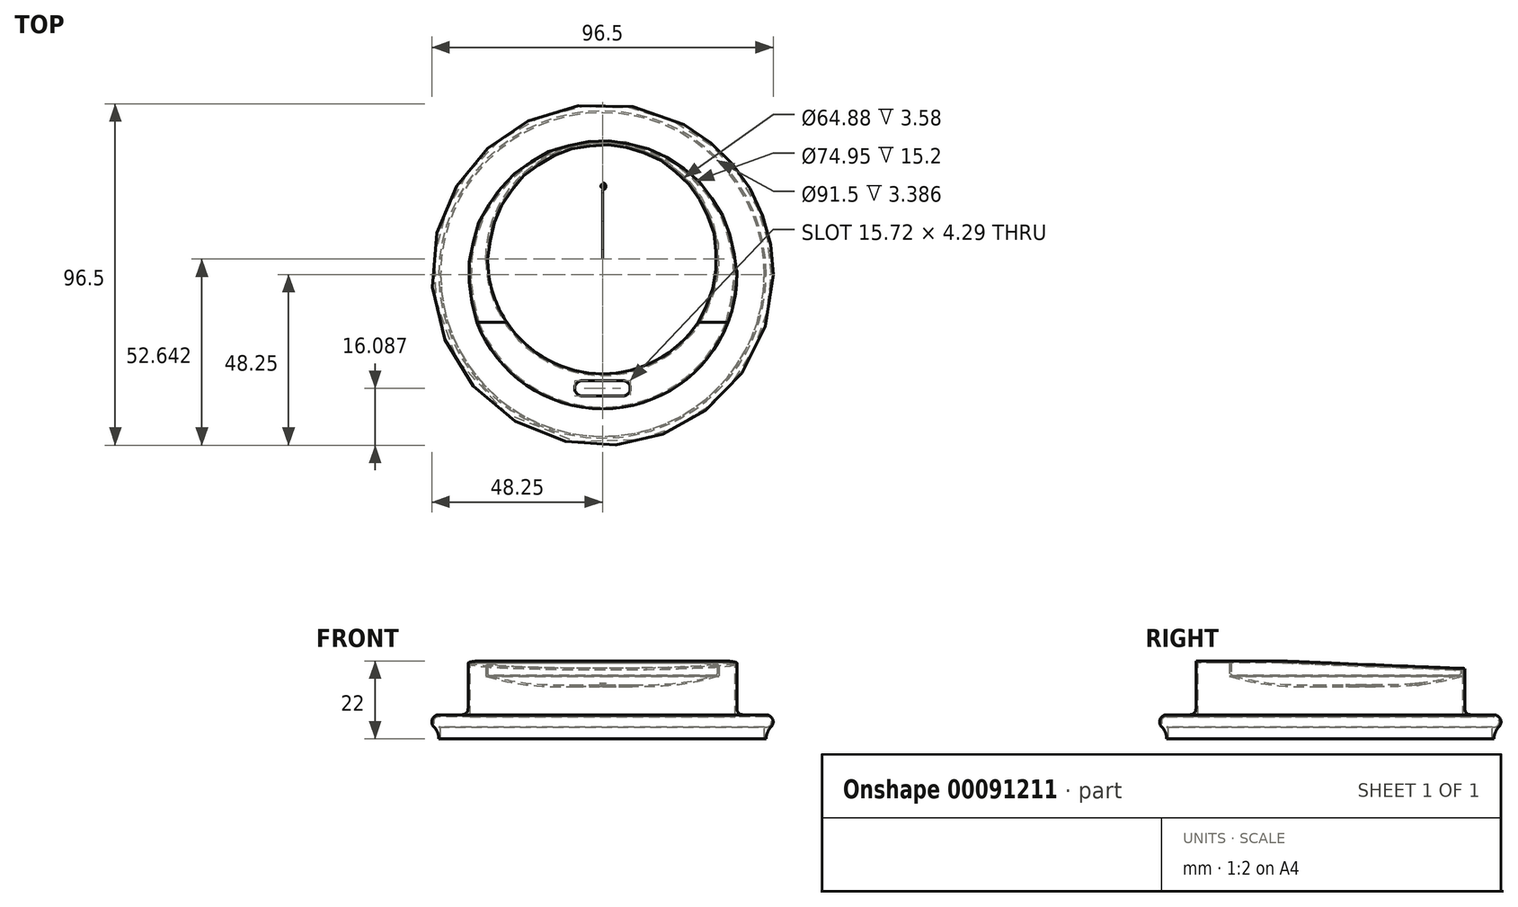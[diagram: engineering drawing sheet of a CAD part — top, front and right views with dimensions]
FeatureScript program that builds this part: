
annotation { "Feature Type Name" : "Feature", "Feature Type Description" : "" }
export const myFeature = defineFeature(function(context is Context, id is Id, definition is map)
    precondition{}
    {
        {
            var Q0;
            Q0=qCreatedBy(makeId("Front.planeOp"),FACE);
            var sketch = newSketch(context, id + "F0", { "sketchPlane" : qUnion([Q0])});
            skLineSegment(sketch, "E0.bottom", {"start": v(46.25, -3.4) * mm, "end": v(-46.25, -3.4) * mm});
            skLineSegment(sketch, "E0.top", {"start": v(46.25, 3.4) * mm, "end": v(-46.25, 3.4) * mm});
            skLineSegment(sketch, "E0.left", {"start": v(46.25, -3.4) * mm, "end": v(46.25, 3.4) * mm});
            skLineSegment(sketch, "E0.right", {"start": v(-46.25, -3.4) * mm, "end": v(-46.25, 3.4) * mm});
            skPoint(sketch, "E0.middle", {"position": v(0, 0) * mm});
            skLineSegment(sketch, "E1.bottom", {"start": v(-38.82, 12.6) * mm, "end": v(37.98, 12.6) * mm});
            skLineSegment(sketch, "E1.top", {"start": v(-38.82, 0) * mm, "end": v(37.98, 0) * mm});
            skLineSegment(sketch, "E1.left", {"start": v(-38.82, 12.6) * mm, "end": v(-38.82, 0) * mm});
            skLineSegment(sketch, "E1.right", {"start": v(37.98, 12.6) * mm, "end": v(37.98, 0) * mm});
            skLineSegment(sketch, "E2", {"start": v(0, 32.32) * mm, "end": v(0, -32.54) * mm});
            skLineSegment(sketch, "E3.bottom", {"start": v(-38.82, 18.6) * mm, "end": v(37.98, 18.6) * mm});
            skLineSegment(sketch, "E3.left", {"start": v(-38.82, 18.6) * mm, "end": v(-38.82, 12.6) * mm});
            skLineSegment(sketch, "E3.right", {"start": v(37.98, 18.6) * mm, "end": v(37.98, 12.6) * mm});
            skArc(sketch, "E4", {"start": v(46.25, -0.6) * mm, "mid": v(48.25, 1.4) * mm, "end": v(46.25, 3.4) * mm});
            skSolve(sketch);
        }
        {
            var Q0;
            {var subQ5=sQuery(id+"F0.wireOp",EDGE,"E3.right");Q0=makeQuery(id+"F0.imprint","IMPRINT",FACE,{"disambiguationData":[TD([[makeQuery(id+"F0.imprint","IMPRINT",EDGE,{"derivedFrom":subQ5}),-1.0]])]});}
            var Q1;
            {var subQ0=sQuery(id+"F0.wireOp",EDGE,"E1.right");var subQ1=sQuery(id+"F0.wireOp",EDGE,"E0.top");var subQ2=makeQuery(id+"F0.imprint","INTERSECT",VERTEX,{"derivedFrom":[subQ1,subQ0]});Q1=makeQuery(id+"F0.imprint","IMPRINT",FACE,{"disambiguationData":[TD([[makeQuery(id+"F0.imprint","IMPRINT",EDGE,{"disambiguationData":[TD([[subQ2,-1.0]])],"derivedFrom":subQ1}),-1.0]])]});}
            var Q2;
            {var subQ0=sQuery(id+"F0.wireOp",EDGE,"E1.right");var subQ1=sQuery(id+"F0.wireOp",EDGE,"E0.top");var subQ2=makeQuery(id+"F0.imprint","INTERSECT",VERTEX,{"derivedFrom":[subQ1,subQ0]});Q2=makeQuery(id+"F0.imprint","IMPRINT",FACE,{"disambiguationData":[TD([[makeQuery(id+"F0.imprint","IMPRINT",EDGE,{"disambiguationData":[TD([[subQ2,-1.0]])],"derivedFrom":subQ1}),1.0]])]});}
            var Q3;
            {var subQ5=sQuery(id+"F0.wireOp",EDGE,"E0.left");Q3=makeQuery(id+"F0.imprint","IMPRINT",FACE,{"disambiguationData":[TD([[makeQuery(id+"F0.imprint","IMPRINT",EDGE,{"derivedFrom":subQ5}),1.0]])]});}
            var Q4;
            {var subQ0=sQuery(id+"F0.wireOp",EDGE,"E4");Q4=makeQuery(id+"F0.imprint","IMPRINT",FACE,{"disambiguationData":[TD([[makeQuery(id+"F0.imprint","IMPRINT",EDGE,{"derivedFrom":subQ0}),1.0]])]});}
            var Q5;
            Q5=sQuery(id+"F0.wireOp",EDGE,"E2");
            revolve(context, id + "F1", {"entities" : qUnion([Q0, Q1, Q2, Q3, Q4]), "axis" : qUnion([Q5]), "revolveType" : RevolveType.FULL});
        }
        {
            var Q0;
            Q0=qCreatedBy(makeId("Right.planeOp"),FACE);
            var sketch = newSketch(context, id + "F2", { "sketchPlane" : qUnion([Q0])});
            skLineSegment(sketch, "E5", {"start": v(4.4, 11.9) * mm, "end": v(4.4, 22.41) * mm});
            skLineSegment(sketch, "E6", {"start": v(4.4, 22.41) * mm, "end": v(36.83, 22.41) * mm});
            skLineSegment(sketch, "E7", {"start": v(36.83, 22.41) * mm, "end": v(36.83, 14.64) * mm});
            skFitSpline(sketch, "E8", {"points": [v(36.83, 14.64) * mm, v(4.4, 11.9) * mm], "startDerivative": vector(-30.26, -8.73) * mm, "endDerivative": vector(-44.97, 0.72) * mm});
            skLineSegment(sketch, "E9", {"start": v(2.77, 11.9) * mm, "end": v(-3.15, 11.9) * mm, "construction": true});
            skSolve(sketch);
        }
        {
            var Q0;
            Q0 = qSketchRegion(id + "F2", true);
            var Q1;
            Q1=sQuery(id+"F2.wireOp",EDGE,"E5");
            revolve(context, id + "F3", {"operationType" : NewBodyOperationType.REMOVE, "entities" : qUnion([Q0]), "axis" : qUnion([Q1]), "revolveType" : RevolveType.FULL});
        }
        {
            var Q0;
            Q0=makeQuery(id+"F1.opRevolve","SWEPT_FACE",FACE,{"disambiguationData":[OSD([sQuery(id+"F0.wireOp",EDGE,"E3.bottom")])]});
            cPlane(context, id + "F4", {"entities" : qUnion([Q0]), "cplaneType" : CPlaneType.OFFSET, "offset" : 0 * mm, "width" : 150 * mm, "height" : 150 * mm});
        }
        {
            var Q0;
            Q0=qCreatedBy(id+"F4.planeOp",FACE);
            var sketch = newSketch(context, id + "F5", { "sketchPlane" : qUnion([Q0])});
            skLineSegment(sketch, "E10", {"start": v(0, -55.1) * mm, "end": v(0, 54.97) * mm});
            skLineSegment(sketch, "E11", {"start": v(-6.37, -30.02) * mm, "end": v(5.72, -30.02) * mm});
            skLineSegment(sketch, "E12", {"start": v(5.72, -34.3) * mm, "end": v(-6.37, -34.3) * mm});
            skArc(sketch, "E13", {"start": v(5.72, -34.3) * mm, "mid": v(7.86, -32.16) * mm, "end": v(5.72, -30.02) * mm});
            skArc(sketch, "E14.MirrorCS", {"start": v(-5.72, -34.3) * mm, "mid": v(-7.86, -32.16) * mm, "end": v(-5.72, -30.02) * mm});
            skCircle(sketch, "E15", {"center": v(0, 25) * mm, "radius": 0.5 * mm});
            skSolve(sketch);
        }
        {
            var Q0;
            Q0=qCreatedBy(makeId("Right.planeOp"),FACE);
            var sketch = newSketch(context, id + "F6", { "sketchPlane" : qUnion([Q0])});
            skLineSegment(sketch, "E16", {"start": v(-19.1, 18.83) * mm, "end": v(39.99, 16.41) * mm});
            skLineSegment(sketch, "E17", {"start": v(39.99, 16.41) * mm, "end": v(39.99, 19.84) * mm});
            skLineSegment(sketch, "E18", {"start": v(39.99, 19.84) * mm, "end": v(-19.1, 19.84) * mm});
            skLineSegment(sketch, "E19", {"start": v(-19.1, 18.83) * mm, "end": v(-19.1, 19.84) * mm});
            skSolve(sketch);
        }
        {
            var Q0;
            Q0=makeQuery(id+"F6.imprint","IMPRINT",FACE,{"disambiguationData":[TD([[makeQuery(id+"F6.imprint","IMPRINT",EDGE,{"derivedFrom":sQuery(id+"F6.wireOp",EDGE,"E16")}),1.0]])]});
            extrude(context, id + "F7", {"entities" : qUnion([Q0]), "operationType" : NewBodyOperationType.REMOVE, "endBound" : BoundingType.SYMMETRIC, "depth" : 90 * mm});
        }
        {
            var Q0;
            Q0=makeQuery(id+"F1.opRevolve","SWEPT_FACE",FACE,{"disambiguationData":[OSD([sQuery(id+"F0.wireOp",EDGE,"E0.bottom")])]});
            shell(context, id + "F8", {"entities" : qUnion([Q0]), "thickness" : .5 * mm});
        }
        {
            var Q0;
            Q0 = qSketchRegion(id + "F5", true);
            extrude(context, id + "F9", {"entities" : qUnion([Q0]), "operationType" : NewBodyOperationType.REMOVE, "oppositeDirection" : true, "depth" : 25 * mm});
        }
        {
            var Q0;
            Q0 = qSketchRegion(id + "F5", true);
            extrude(context, id + "F10", {"entities" : qUnion([Q0]), "operationType" : NewBodyOperationType.REMOVE, "oppositeDirection" : true, "depth" : 25 * mm});
        }
        {
            var Q0;
            Q0=makeQuery(id+"F1.opRevolve","SWEPT_FACE",FACE,{"disambiguationData":[OSD([sQuery(id+"F0.wireOp",EDGE,"E0.top")])]});
            fillet(context, id + "F11", {"entities" : qUnion([Q0]), "radius" : 2 * mm, "tangentPropagation" : true, "rho" : 0.5, "crossSection" : FilletCrossSection.CONIC, "allowEdgeOverflow" : false});
        }
        {
            var Q0;
            Q0=makeQuery(id+"F3.boolean.opBoolean","COPY",FACE,{"derivedFrom":makeQuery(id+"F3.opRevolve","SWEPT_FACE",FACE,{"disambiguationData":[OSD([sQuery(id+"F2.wireOp",EDGE,"E8")])]})});
            fillet(context, id + "F12", {"entities" : qUnion([Q0]), "radius" : .5 * mm, "tangentPropagation" : true, "allowEdgeOverflow" : false});
        }
        {
            var Q0;
            Q0=makeQuery(id+"F1.opRevolve","SWEPT_FACE",FACE,{"disambiguationData":[OSD([sQuery(id+"F0.wireOp",EDGE,"E4")])]});
            fillet(context, id + "F13", {"entities" : qUnion([Q0]), "radius" : 5 * mm, "tangentPropagation" : true, "allowEdgeOverflow" : false});
        }
    });
